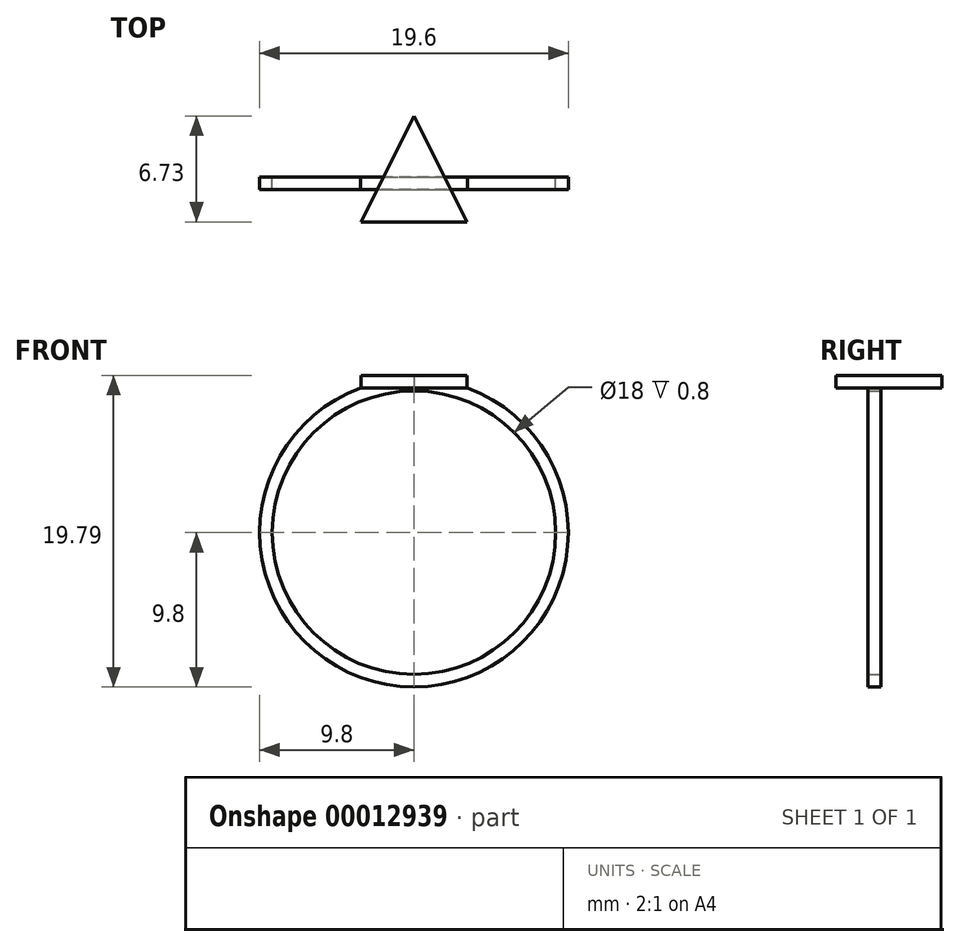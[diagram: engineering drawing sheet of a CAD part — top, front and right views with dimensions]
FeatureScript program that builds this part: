
annotation { "Feature Type Name" : "Feature", "Feature Type Description" : "" }
export const myFeature = defineFeature(function(context is Context, id is Id, definition is map)
    precondition{}
    {
        {
            var Q0;
            Q0=qCreatedBy(makeId("Front.planeOp"),FACE);
            var sketch = newSketch(context, id + "F0", { "sketchPlane" : qUnion([Q0])});
            skCircle(sketch, "E0", {"center": v(0, 0) * mm, "radius": 9 * mm});
            skCircle(sketch, "E1", {"center": v(0, 0) * mm, "radius": 9.8 * mm});
            skLineSegment(sketch, "E2", {"start": v(-3.4, 9.19) * mm, "end": v(3.4, 9.19) * mm});
            skLineSegment(sketch, "E3", {"start": v(0, 0) * mm, "end": v(3.4, 9.19) * mm});
            skLineSegment(sketch, "E4", {"start": v(-3.4, 9.19) * mm, "end": v(0, 0) * mm});
            skSolve(sketch);
        }
        {
            var Q0;
            {var subQ1=sQuery(id+"F0.wireOp",EDGE,"E0");var subQ6=sQuery(id+"F0.wireOp",EDGE,"E3");var subQ7=makeQuery(id+"F0.imprint","INTERSECT",VERTEX,{"derivedFrom":[subQ1,subQ6]});Q0=makeQuery(id+"F0.imprint","IMPRINT",FACE,{"disambiguationData":[TD([[makeQuery(id+"F0.imprint","IMPRINT",EDGE,{"disambiguationData":[TD([[subQ7,1.0]])],"derivedFrom":subQ1}),-1.0]])]});}
            var Q1;
            {var subQ4=sQuery(id+"F0.wireOp",EDGE,"E2");Q1=makeQuery(id+"F0.imprint","IMPRINT",FACE,{"disambiguationData":[TD([[makeQuery(id+"F0.imprint","IMPRINT",EDGE,{"derivedFrom":subQ4}),-1.0]])]});}
            extrude(context, id + "F1", {"entities" : qUnion([Q0, Q1]), "depth" : .4 * mm, "hasSecondDirection" : true, "secondDirectionOppositeDirection" : true, "secondDirectionDepth" : .4 * mm});
        }
        {
            var Q0;
            Q0=makeQuery(id+"F1.opExtrude","SWEPT_FACE",FACE,{"disambiguationData":[OSD([sQuery(id+"F0.wireOp",EDGE,"E2")])]});
            var sketch = newSketch(context, id + "F2", { "sketchPlane" : qUnion([Q0])});
            skLineSegment(sketch, "E5.rect.bottom", {"start": v(3.37, -2.46) * mm, "end": v(-3.37, -2.46) * mm});
            skPoint(sketch, "E5.rect.middle", {"position": v(0, 0) * mm});
            skLineSegment(sketch, "E6", {"start": v(-3.37, -2.46) * mm, "end": v(0, 4.27) * mm});
            skLineSegment(sketch, "E7", {"start": v(0, 4.27) * mm, "end": v(3.37, -2.46) * mm});
            skSolve(sketch);
        }
        {
            var Q0;
            Q0=qSketchRegion(id+"F2",true);
            extrude(context, id + "F3", {"entities" : qUnion([Q0]), "operationType" : NewBodyOperationType.ADD, "depth" : .8 * mm});
        }
    });
